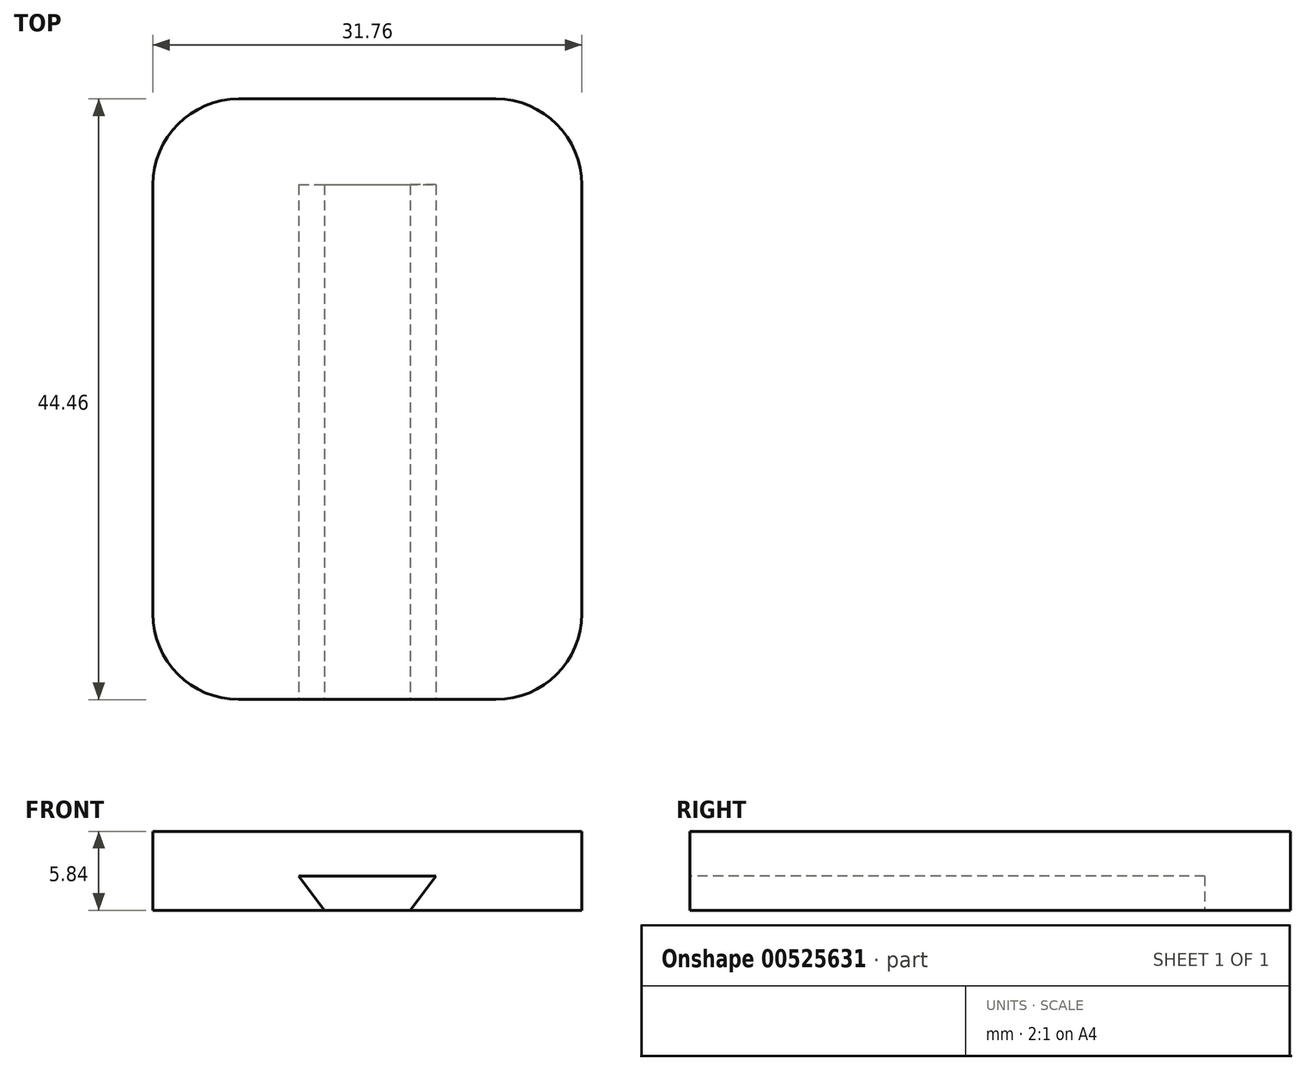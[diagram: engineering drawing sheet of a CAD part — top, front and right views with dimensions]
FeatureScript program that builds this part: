
annotation { "Feature Type Name" : "Feature", "Feature Type Description" : "" }
export const myFeature = defineFeature(function(context is Context, id is Id, definition is map)
    precondition{}
    {
        {
            var Q0;
            Q0=qCreatedBy(makeId("Top.planeOp"),FACE);
            var sketch = newSketch(context, id + "F0", { "sketchPlane" : qUnion([Q0])});
            skLineSegment(sketch, "E0.bottom", {"start": v(-15.88, 22.23) * mm, "end": v(15.88, 22.23) * mm});
            skLineSegment(sketch, "E0.top", {"start": v(-15.88, -22.23) * mm, "end": v(15.88, -22.23) * mm});
            skLineSegment(sketch, "E0.left", {"start": v(-15.88, 22.23) * mm, "end": v(-15.88, -22.22) * mm});
            skLineSegment(sketch, "E0.right", {"start": v(15.88, 22.23) * mm, "end": v(15.88, -22.22) * mm});
            skSolve(sketch);
        }
        {
            var Q0;
            Q0=makeQuery(id+"F0.imprint","IMPRINT",FACE,{"disambiguationData":[TD([[makeQuery(id+"F0.imprint","IMPRINT",EDGE,{"derivedFrom":sQuery(id+"F0.wireOp",EDGE,"E0.bottom")}),-1.0]])]});
            extrude(context, id + "F1", {"entities" : qUnion([Q0]), "depth" : 5.84 * mm});
        }
        {
            var Q0;
            Q0=makeQuery(id+"F1.opExtrude","SWEPT_EDGE",EDGE,{"disambiguationData":[OSD([sQuery(id+"F0.wireOp",EDGE,"E0.bottom"),sQuery(id+"F0.wireOp",EDGE,"E0.right")])]});
            var Q1;
            Q1=makeQuery(id+"F1.opExtrude","SWEPT_EDGE",EDGE,{"disambiguationData":[OSD([sQuery(id+"F0.wireOp",EDGE,"E0.bottom"),sQuery(id+"F0.wireOp",EDGE,"E0.left")])]});
            var Q2;
            Q2=makeQuery(id+"F1.opExtrude","SWEPT_EDGE",EDGE,{"disambiguationData":[OSD([sQuery(id+"F0.wireOp",EDGE,"E0.top"),sQuery(id+"F0.wireOp",EDGE,"E0.left")])]});
            var Q3;
            Q3=makeQuery(id+"F1.opExtrude","SWEPT_EDGE",EDGE,{"disambiguationData":[OSD([sQuery(id+"F0.wireOp",EDGE,"E0.top"),sQuery(id+"F0.wireOp",EDGE,"E0.right")])]});
            fillet(context, id + "F2", {"entities" : qUnion([Q0, Q1, Q2, Q3]), "radius" : 6.35 * mm, "tangentPropagation" : true, "allowEdgeOverflow" : false});
        }
        {
            var Q0;
            Q0=makeQuery(id+"F1.opExtrude","SWEPT_FACE",FACE,{"disambiguationData":[OSD([sQuery(id+"F0.wireOp",EDGE,"E0.top")])]});
            var sketch = newSketch(context, id + "F3", { "sketchPlane" : qUnion([Q0])});
            skPoint(sketch, "E1.endSnap0", {"position": v(0, 0) * mm});
            skLineSegment(sketch, "E2", {"start": v(0, 2.54) * mm, "end": v(5.08, 2.54) * mm});
            skLineSegment(sketch, "E3", {"start": v(5.08, 2.54) * mm, "end": v(3.18, 0) * mm});
            skLineSegment(sketch, "E4", {"start": v(0, 2.54) * mm, "end": v(-5.08, 2.54) * mm});
            skLineSegment(sketch, "E5", {"start": v(-5.08, 2.54) * mm, "end": v(-3.18, 0) * mm});
            skSolve(sketch);
        }
        {
            var Q0;
            Q0=makeQuery(id+"F3.imprint","IMPRINT",FACE,{"disambiguationData":[TD([[makeQuery(id+"F3.imprint","IMPRINT",EDGE,{"derivedFrom":sQuery(id+"F3.wireOp",EDGE,"E2")}),-1.0]])]});
            extrude(context, id + "F4", {"entities" : qUnion([Q0]), "operationType" : NewBodyOperationType.REMOVE, "oppositeDirection" : true, "depth" : 38.1 * mm});
        }
    });
